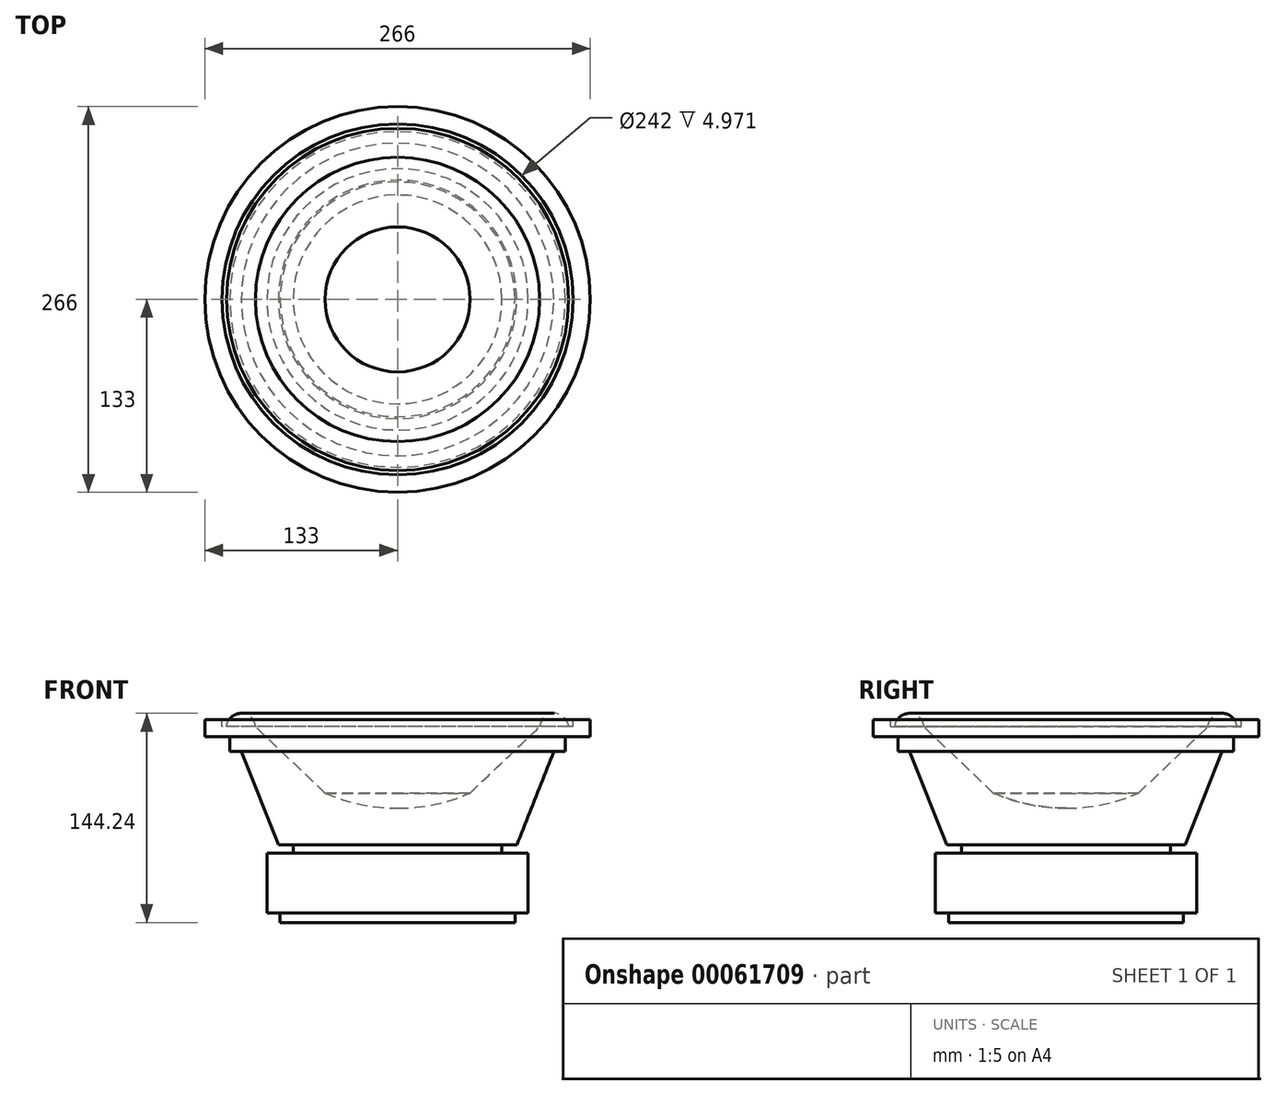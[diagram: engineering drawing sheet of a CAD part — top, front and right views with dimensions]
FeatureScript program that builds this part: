
annotation { "Feature Type Name" : "Feature", "Feature Type Description" : "" }
export const myFeature = defineFeature(function(context is Context, id is Id, definition is map)
    precondition{}
    {
        {
            var Q0;
            Q0=qCreatedBy(makeId("Right.planeOp"),FACE);
            var sketch = newSketch(context, id + "F0", { "sketchPlane" : qUnion([Q0])});
            skLineSegment(sketch, "E0", {"start": v(0, -10.44) * mm, "end": v(0, -89.24) * mm});
            skLineSegment(sketch, "E1", {"start": v(-50, 0) * mm, "end": v(-98.03, 45.8) * mm});
            skArc(sketch, "E2", {"start": v(-98.03, 45.8) * mm, "mid": v(-108, 55) * mm, "end": v(-117.97, 45.8) * mm});
            skLineSegment(sketch, "E3", {"start": v(-117.97, 45.8) * mm, "end": v(-121, 45.8) * mm});
            skLineSegment(sketch, "E4", {"start": v(-121, 45.8) * mm, "end": v(-121, 50.76) * mm});
            skLineSegment(sketch, "E5", {"start": v(-121, 50.76) * mm, "end": v(-133, 50.76) * mm});
            skLineSegment(sketch, "E6", {"start": v(-133, 50.76) * mm, "end": v(-133, 38.76) * mm});
            skLineSegment(sketch, "E7", {"start": v(-133, 38.76) * mm, "end": v(-115.75, 38.76) * mm});
            skLineSegment(sketch, "E8", {"start": v(-115.75, 38.76) * mm, "end": v(-115.75, 28.76) * mm});
            skLineSegment(sketch, "E9", {"start": v(-115.75, 28.76) * mm, "end": v(-107.78, 28.76) * mm});
            skLineSegment(sketch, "E10", {"start": v(-107.78, 28.76) * mm, "end": v(-82.25, -35.76) * mm});
            skLineSegment(sketch, "E11", {"start": v(-82.25, -35.76) * mm, "end": v(-72.04, -35.76) * mm});
            skLineSegment(sketch, "E12", {"start": v(-72.04, -35.76) * mm, "end": v(-72.04, -41.5) * mm});
            skLineSegment(sketch, "E13", {"start": v(-72.04, -41.5) * mm, "end": v(-90.14, -41.5) * mm});
            skLineSegment(sketch, "E14", {"start": v(-90.14, -41.5) * mm, "end": v(-90.14, -82.74) * mm});
            skLineSegment(sketch, "E15", {"start": v(-90.14, -82.74) * mm, "end": v(-81, -82.74) * mm});
            skLineSegment(sketch, "E16", {"start": v(-81, -82.74) * mm, "end": v(-81, -89.24) * mm});
            skLineSegment(sketch, "E17", {"start": v(-81, -89.24) * mm, "end": v(0, -89.24) * mm});
            skArc(sketch, "E18", {"start": v(-50, 0) * mm, "mid": v(-25.54, -7.8) * mm, "end": v(0, -10.44) * mm});
            skSolve(sketch);
        }
        {
            var Q0;
            Q0=makeQuery(id+"F0.imprint","IMPRINT",FACE,{"disambiguationData":[TD([[makeQuery(id+"F0.imprint","IMPRINT",EDGE,{"derivedFrom":sQuery(id+"F0.wireOp",EDGE,"E0")}),-1.0]])]});
            var Q1;
            Q1=sQuery(id+"F0.wireOp",EDGE,"E0");
            revolve(context, id + "F1", {"entities" : qUnion([Q0]), "axis" : qUnion([Q1]), "revolveType" : RevolveType.FULL});
        }
    });
